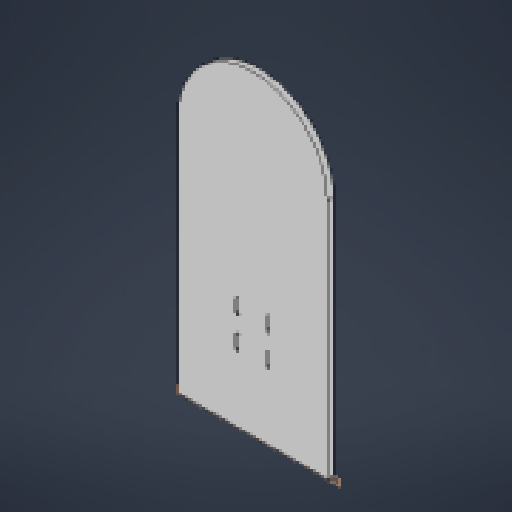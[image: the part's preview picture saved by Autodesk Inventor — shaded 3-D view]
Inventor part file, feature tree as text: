
AUTODESK INVENTOR PART (.ipt)
format: ipt  version: 2024 (Build 280153000, 153)  size: 182,784 bytes
history: native  units: in
note: dims shown in document units (in); Inventor stores cm internally (conversion verified against a paired STEP export)
features: other x9, reference x3, plane x1, sketch x1, extrude x1
ambient origin geometry x8: Origin, YZ Plane, XZ Plane, XY Plane, X Axis, Y Axis, Z Axis, Center Point
bodies: Solid1 (feature_tree)
feature tree (15):
  plane  "Work Plane1"
  sketch  "Sketch1"  dims[d0=2.0in d1=6.0in d2=1.22in d3=1.22in d4=0.25in d5=0.1181in d6=0.25in d7=0.1181in d8=0.25in d9=0.1181in d10=0.25in d11=0.1181in d12=0.25in d13=0.0in d14=0.1969in d15=1.5748in d17=360.0deg d19=0.25in]
  extrude  "Extrusion1"  Depth=0.25in
  other  "Work Point1"
  reference  "Reference1"
  reference  "Reference2"
  reference  "Reference3"
  other  "<userpath>\CodingProjects\C-AAM\CAD\V1\Parts\2ndAxis.iam"
  other  "2ndAxis.iam"
  other  "AxisBoard:1"
  other  "<userpath>\CodingProjects\C-AAM\CAD\V1\Base.iam"
  other  "Base.iam"
  other  "6627T91_Stepper Motor:1"
  other  "LazySusan:1"
  other  "OR:1"
